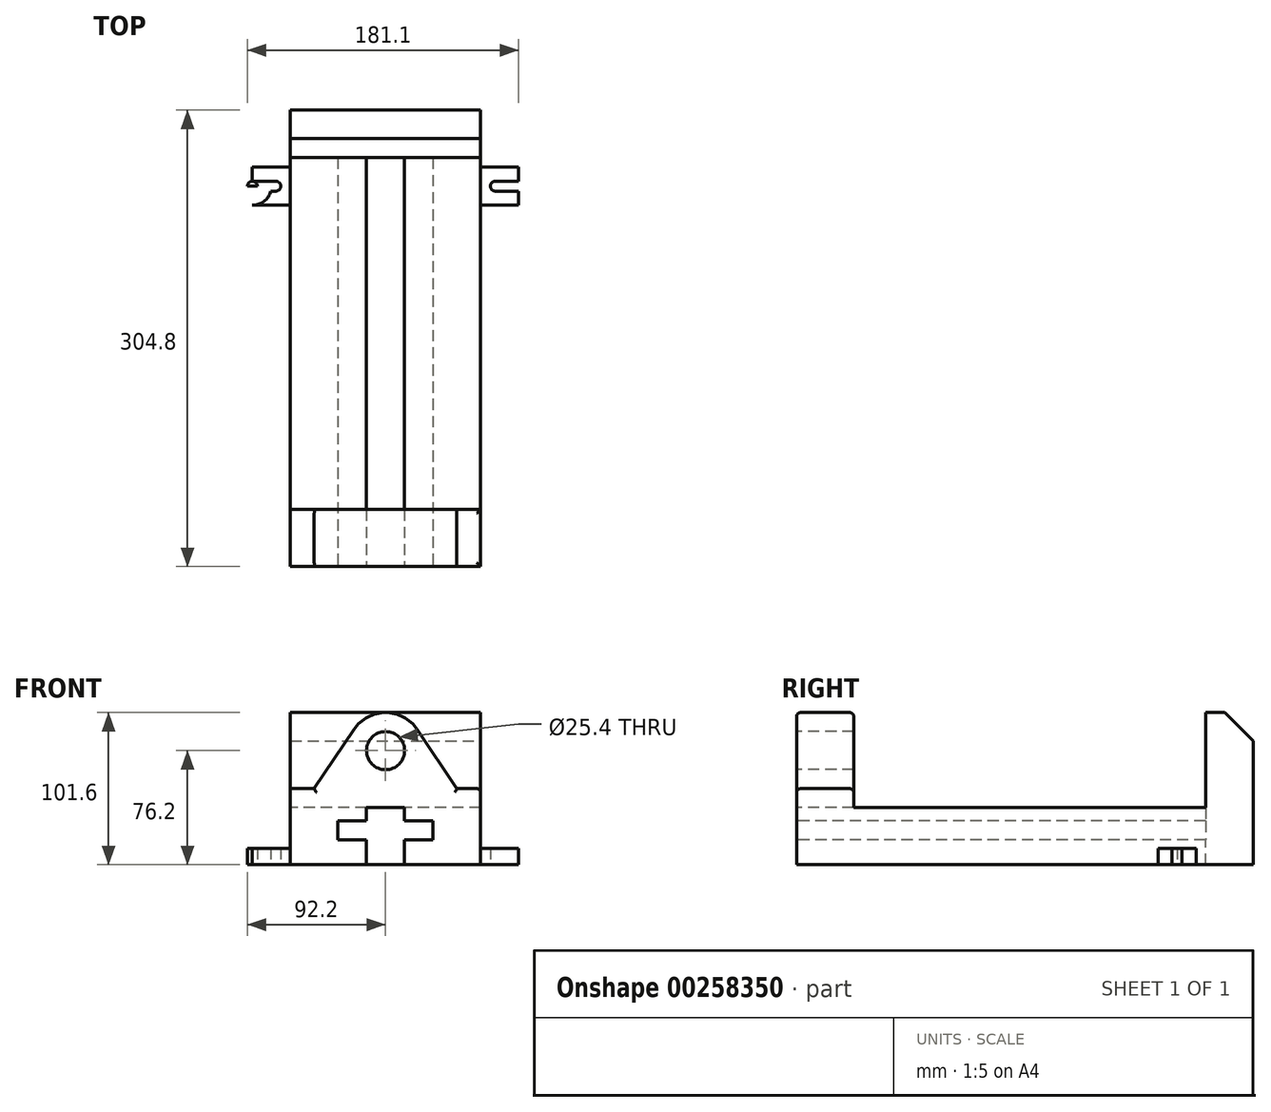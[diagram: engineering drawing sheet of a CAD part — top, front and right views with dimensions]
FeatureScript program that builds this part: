
annotation { "Feature Type Name" : "Feature", "Feature Type Description" : "" }
export const myFeature = defineFeature(function(context is Context, id is Id, definition is map)
    precondition{}
    {
        {
            var Q0;
            Q0=qCreatedBy(makeId("Top.planeOp"),FACE);
            var sketch = newSketch(context, id + "F0", { "sketchPlane" : qUnion([Q0])});
            skLineSegment(sketch, "E0.bottom", {"start": v(63.5, -152.4) * mm, "end": v(-63.5, -152.4) * mm});
            skLineSegment(sketch, "E0.top", {"start": v(63.5, 152.4) * mm, "end": v(-63.5, 152.4) * mm});
            skLineSegment(sketch, "E0.left", {"start": v(63.5, -152.4) * mm, "end": v(63.5, 152.4) * mm});
            skLineSegment(sketch, "E0.right", {"start": v(-63.5, -152.4) * mm, "end": v(-63.5, 152.4) * mm});
            skPoint(sketch, "E0.middle", {"position": v(0, 0) * mm});
            skLineSegment(sketch, "E1", {"start": v(-63.5, 152.4) * mm, "end": v(-63.5, 101.6) * mm});
            skPoint(sketch, "E2.startSnap0", {"position": v(0, 152.4) * mm});
            skLineSegment(sketch, "E3", {"start": v(-63.5, 101.6) * mm, "end": v(-101.6, 101.6) * mm});
            skLineSegment(sketch, "E4", {"start": v(63.5, 101.6) * mm, "end": v(101.6, 101.6) * mm});
            skLineSegment(sketch, "E5", {"start": v(-101.6, 101.6) * mm, "end": v(-88.9, 101.6) * mm});
            skCircle(sketch, "E6", {"center": v(-88.9, 101.6) * mm, "radius": 12.7 * mm});
            skLineSegment(sketch, "E7", {"start": v(-88.9, 101.6) * mm, "end": v(-88.9, 88.9) * mm});
            skLineSegment(sketch, "E8", {"start": v(-88.9, 88.9) * mm, "end": v(-88.9, 101.6) * mm});
            skLineSegment(sketch, "E9", {"start": v(-88.9, 114.3) * mm, "end": v(-88.9, 101.6) * mm});
            skLineSegment(sketch, "E10", {"start": v(-88.9, 88.9) * mm, "end": v(-63.5, 88.9) * mm});
            skLineSegment(sketch, "E11", {"start": v(-88.9, 114.3) * mm, "end": v(-63.5, 114.3) * mm});
            skLineSegment(sketch, "E12", {"start": v(-88.9, 101.6) * mm, "end": v(-88.9, 98.3) * mm});
            skLineSegment(sketch, "E13", {"start": v(-88.9, 98.3) * mm, "end": v(-88.9, 104.9) * mm});
            skCircle(sketch, "E14", {"center": v(-88.9, 101.6) * mm, "radius": 3.3 * mm});
            skLineSegment(sketch, "E15", {"start": v(-88.9, 98.3) * mm, "end": v(-73.28, 98.3) * mm});
            skLineSegment(sketch, "E16", {"start": v(-88.9, 104.9) * mm, "end": v(-73.28, 104.9) * mm});
            skCircle(sketch, "E17", {"center": v(-73.28, 101.6) * mm, "radius": 3.3 * mm});
            skLineSegment(sketch, "E18", {"start": v(101.6, 101.6) * mm, "end": v(88.9, 101.6) * mm});
            skCircle(sketch, "E19", {"center": v(88.9, 101.6) * mm, "radius": 12.7 * mm});
            skCircle(sketch, "E20", {"center": v(88.9, 101.6) * mm, "radius": 3.3 * mm});
            skLineSegment(sketch, "E21", {"start": v(88.9, 101.6) * mm, "end": v(88.9, 88.9) * mm});
            skLineSegment(sketch, "E22", {"start": v(88.9, 88.9) * mm, "end": v(63.5, 88.9) * mm});
            skLineSegment(sketch, "E23", {"start": v(88.9, 101.6) * mm, "end": v(88.9, 114.3) * mm});
            skLineSegment(sketch, "E24", {"start": v(88.9, 114.3) * mm, "end": v(63.5, 114.3) * mm});
            skLineSegment(sketch, "E25", {"start": v(88.9, 101.6) * mm, "end": v(73.28, 101.6) * mm});
            skCircle(sketch, "E26", {"center": v(73.28, 101.6) * mm, "radius": 3.3 * mm});
            skLineSegment(sketch, "E27", {"start": v(73.28, 101.6) * mm, "end": v(73.28, 98.3) * mm});
            skLineSegment(sketch, "E28", {"start": v(73.28, 98.3) * mm, "end": v(88.9, 98.3) * mm});
            skLineSegment(sketch, "E29", {"start": v(73.28, 98.3) * mm, "end": v(73.28, 104.9) * mm});
            skLineSegment(sketch, "E30", {"start": v(73.28, 104.9) * mm, "end": v(88.9, 104.9) * mm});
            skSolve(sketch);
        }
        {
            var Q0;
            Q0=makeQuery(id+"F0.imprint","IMPRINT",FACE,{"disambiguationData":[TD([[makeQuery(id+"F0.imprint","IMPRINT",EDGE,{"derivedFrom":sQuery(id+"F0.wireOp",EDGE,"E0.bottom")}),-1.0]])]});
            extrude(context, id + "F1", {"entities" : qUnion([Q0]), "depth" : 38.1 * mm});
        }
        {
            var Q0;
            Q0=makeQuery(id+"F1.opExtrude","SWEPT_FACE",FACE,{"disambiguationData":[OSD([sQuery(id+"F0.wireOp",EDGE,"E0.bottom")])]});
            var sketch = newSketch(context, id + "F2", { "sketchPlane" : qUnion([Q0])});
            skLineSegment(sketch, "E31", {"start": v(0, 0) * mm, "end": v(12.7, 0) * mm});
            skLineSegment(sketch, "E32", {"start": v(0, 0) * mm, "end": v(-12.7, 0) * mm});
            skLineSegment(sketch, "E33", {"start": v(-12.7, 0) * mm, "end": v(-12.7, 16.51) * mm});
            skLineSegment(sketch, "E34", {"start": v(-12.7, 16.51) * mm, "end": v(-31.75, 16.51) * mm});
            skLineSegment(sketch, "E35", {"start": v(-31.75, 16.51) * mm, "end": v(-31.75, 29.21) * mm});
            skLineSegment(sketch, "E36", {"start": v(-31.75, 29.21) * mm, "end": v(-12.7, 29.21) * mm});
            skLineSegment(sketch, "E37", {"start": v(-12.7, 29.21) * mm, "end": v(-12.7, 38.1) * mm});
            skLineSegment(sketch, "E38", {"start": v(-12.7, 38.1) * mm, "end": v(12.7, 38.1) * mm});
            skLineSegment(sketch, "E39", {"start": v(12.7, 38.1) * mm, "end": v(12.7, 29.21) * mm});
            skLineSegment(sketch, "E40", {"start": v(12.7, 29.21) * mm, "end": v(31.75, 29.21) * mm});
            skLineSegment(sketch, "E41", {"start": v(31.75, 29.21) * mm, "end": v(31.75, 16.51) * mm});
            skLineSegment(sketch, "E42", {"start": v(31.75, 16.51) * mm, "end": v(12.7, 16.51) * mm});
            skLineSegment(sketch, "E43", {"start": v(12.7, 16.51) * mm, "end": v(12.7, 0) * mm});
            skSolve(sketch);
        }
        {
            var Q0;
            Q0 = qSketchRegion(id + "F2", true);
            extrude(context, id + "F3", {"entities" : qUnion([Q0]), "operationType" : NewBodyOperationType.REMOVE, "oppositeDirection" : true, "depth" : 273.05 * mm});
        }
        {
            var Q0;
            Q0=makeQuery(id+"F1.opExtrude","CAP_FACE",FACE,{"disambiguationData":[OSD([sQuery(id+"F0.wireOp",EDGE,"E0.bottom"),sQuery(id+"F0.wireOp",EDGE,"E0.top"),sQuery(id+"F0.wireOp",EDGE,"E0.left"),sQuery(id+"F0.wireOp",EDGE,"E0.right")])],"isStart":false});
            var sketch = newSketch(context, id + "F4", { "sketchPlane" : qUnion([Q0])});
            skLineSegment(sketch, "E44.bottom", {"start": v(-63.5, -152.4) * mm, "end": v(63.5, -152.4) * mm});
            skLineSegment(sketch, "E44.top", {"start": v(-63.5, -114.3) * mm, "end": v(63.5, -114.3) * mm});
            skLineSegment(sketch, "E44.left", {"start": v(-63.5, -152.4) * mm, "end": v(-63.5, -114.3) * mm});
            skLineSegment(sketch, "E44.right", {"start": v(63.5, -152.4) * mm, "end": v(63.5, -114.3) * mm});
            skLineSegment(sketch, "E45.top", {"start": v(-63.5, -184.15) * mm, "end": v(63.5, -184.15) * mm});
            skLineSegment(sketch, "E45.left", {"start": v(-63.5, -152.4) * mm, "end": v(-63.5, -184.15) * mm});
            skLineSegment(sketch, "E45.right", {"start": v(63.5, -152.4) * mm, "end": v(63.5, -184.15) * mm});
            skSolve(sketch);
        }
        {
            var Q0;
            {var subQ0=sQuery(id+"F4.wireOp",EDGE,"E44.bottom");var subQ1=sQuery(id+"F2.wireOp",EDGE,"E38");var subQ2=sQuery(id+"F0.wireOp",EDGE,"E0.bottom");var subQ3=makeQuery(id+"F3.boolean.opBoolean","COPY",EDGE,{"derivedFrom":makeQuery(id+"F3.opExtrude","SWEPT_EDGE",EDGE,{"disambiguationData":[OSD([subQ2,sQuery(id+"F2.wireOp",EDGE,"E37"),subQ1])]})});var subQ4=makeQuery(id+"F4.imprint","INTERSECT",VERTEX,{"derivedFrom":[subQ3,subQ0]});var subQ5=makeQuery(id+"F3.boolean.opBoolean","COPY",EDGE,{"derivedFrom":makeQuery(id+"F3.opExtrude","SWEPT_EDGE",EDGE,{"disambiguationData":[OSD([subQ2,subQ1,sQuery(id+"F2.wireOp",EDGE,"E39")])]})});var subQ6=makeQuery(id+"F4.imprint","INTERSECT",VERTEX,{"derivedFrom":[subQ5,subQ0]});Q0=makeQuery(id+"F4.imprint","IMPRINT",FACE,{"disambiguationData":[TD([[makeQuery(id+"F4.imprint","IMPRINT",EDGE,{"disambiguationData":[TD([[subQ4,-1.0],[subQ6,1.0]])],"derivedFrom":subQ0}),1.0]])]});}
            var Q1;
            {var subQ0=sQuery(id+"F4.wireOp",EDGE,"E44.left");Q1=makeQuery(id+"F4.imprint","IMPRINT",FACE,{"disambiguationData":[TD([[makeQuery(id+"F4.imprint","IMPRINT",EDGE,{"derivedFrom":subQ0}),-1.0]])]});}
            var Q2;
            {var subQ0=sQuery(id+"F4.wireOp",EDGE,"E44.right");Q2=makeQuery(id+"F4.imprint","IMPRINT",FACE,{"disambiguationData":[TD([[makeQuery(id+"F4.imprint","IMPRINT",EDGE,{"derivedFrom":subQ0}),1.0]])]});}
            extrude(context, id + "F5", {"entities" : qUnion([Q0, Q1, Q2]), "operationType" : NewBodyOperationType.ADD, "depth" : 12.7 * mm});
        }
        {
            var Q0;
            {var subQ0=sQuery(id+"F0.wireOp",EDGE,"E0.right");var subQ1=sQuery(id+"F0.wireOp",EDGE,"E0.left");var subQ3=sQuery(id+"F0.wireOp",EDGE,"E0.bottom");var subQ6=makeQuery(id+"F1.opExtrude","SWEPT_FACE",FACE,{"disambiguationData":[OSD([subQ3])]});Q0=makeQuery(id+"F5.boolean.opBoolean","MERGE",FACE,{"derivedFrom":[makeQuery(id+"F3.boolean.opBoolean","SPLIT",FACE,{"disambiguationData":[TD([makeQuery(id+"F1.opExtrude","SWEPT_FACE",FACE,{"disambiguationData":[OSD([subQ1])]})])],"derivedFrom":subQ6}),makeQuery(id+"F3.boolean.opBoolean","SPLIT",FACE,{"disambiguationData":[TD([makeQuery(id+"F1.opExtrude","SWEPT_FACE",FACE,{"disambiguationData":[OSD([subQ0])]})])],"derivedFrom":subQ6}),makeQuery(id+"F5.opExtrude","SWEPT_FACE",FACE,{"disambiguationData":[OSD([sQuery(id+"F4.wireOp",EDGE,"E44.bottom")])]})]});}
            var sketch = newSketch(context, id + "F6", { "sketchPlane" : qUnion([Q0])});
            skLineSegment(sketch, "E46", {"start": v(0, 0) * mm, "end": v(0, 76.2) * mm});
            skPoint(sketch, "E46.endSnap0", {"position": v(0, 50.8) * mm});
            skCircle(sketch, "E47", {"center": v(0, 76.2) * mm, "radius": 12.7 * mm});
            skLineSegment(sketch, "E48", {"start": v(-63.5, 50.8) * mm, "end": v(-47.63, 50.8) * mm});
            skLineSegment(sketch, "E49", {"start": v(63.5, 50.8) * mm, "end": v(47.62, 50.8) * mm});
            skLineSegment(sketch, "E50", {"start": v(47.62, 50.8) * mm, "end": v(21.1, 90.35) * mm});
            skLineSegment(sketch, "E51", {"start": v(-47.63, 50.8) * mm, "end": v(-21.1, 90.35) * mm});
            skArc(sketch, "E52", {"start": v(21.1, 90.35) * mm, "mid": v(0, 101.6) * mm, "end": v(-21.1, 90.35) * mm});
            skLineSegment(sketch, "E53", {"start": v(-63.5, 50.8) * mm, "end": v(-63.5, 38.1) * mm});
            skLineSegment(sketch, "E54", {"start": v(-63.5, 38.1) * mm, "end": v(12.7, 38.1) * mm});
            skPoint(sketch, "E54.endSnap0", {"position": v(12.7, 40) * mm});
            skSolve(sketch);
        }
        {
            var Q0;
            Q0=makeQuery(id+"F6.imprint","IMPRINT",FACE,{"disambiguationData":[TD([[makeQuery(id+"F6.imprint","IMPRINT",EDGE,{"derivedFrom":sQuery(id+"F6.wireOp",EDGE,"E47")}),-1.0]])]});
            extrude(context, id + "F7", {"entities" : qUnion([Q0]), "operationType" : NewBodyOperationType.ADD, "oppositeDirection" : true, "depth" : 38.1 * mm});
        }
        {
            var Q0;
            Q0=makeQuery(id+"F5.opExtrude","CAP_EDGE",EDGE,{"disambiguationData":[OSD([sQuery(id+"F4.wireOp",EDGE,"E44.bottom")])],"isStart":false});
            var Q1;
            Q1=makeQuery(id+"F7.opExtrude","CAP_EDGE",EDGE,{"disambiguationData":[OSD([sQuery(id+"F6.wireOp",EDGE,"E50")])],"isStart":true});
            var Q2;
            Q2=makeQuery(id+"F5.opExtrude","CAP_EDGE",EDGE,{"disambiguationData":[OSD([sQuery(id+"F4.wireOp",EDGE,"E44.right")])],"isStart":false});
            var Q3;
            Q3=makeQuery(id+"F5.opExtrude","CAP_EDGE",EDGE,{"disambiguationData":[OSD([sQuery(id+"F4.wireOp",EDGE,"E44.top")])],"isStart":false});
            var Q4;
            Q4=makeQuery(id+"F7.opExtrude","CAP_EDGE",EDGE,{"disambiguationData":[OSD([sQuery(id+"F6.wireOp",EDGE,"E50")])],"isStart":false});
            var Q5;
            Q5=makeQuery(id+"F7.opExtrude","CAP_EDGE",EDGE,{"disambiguationData":[OSD([sQuery(id+"F6.wireOp",EDGE,"E52")])],"isStart":true});
            var Q6;
            Q6=makeQuery(id+"F7.opExtrude","CAP_EDGE",EDGE,{"disambiguationData":[OSD([sQuery(id+"F6.wireOp",EDGE,"E52")])],"isStart":false});
            var Q7;
            Q7=makeQuery(id+"F7.opExtrude","CAP_EDGE",EDGE,{"disambiguationData":[OSD([sQuery(id+"F6.wireOp",EDGE,"E51")])],"isStart":true});
            var Q8;
            Q8=makeQuery(id+"F7.opExtrude","CAP_EDGE",EDGE,{"disambiguationData":[OSD([sQuery(id+"F6.wireOp",EDGE,"E51")])],"isStart":false});
            var Q9;
            Q9=makeQuery(id+"F7.opExtrude","CAP_EDGE",EDGE,{"disambiguationData":[OSD([sQuery(id+"F6.wireOp",EDGE,"E48")])],"isStart":true});
            var Q10;
            Q10=makeQuery(id+"F7.opExtrude","CAP_EDGE",EDGE,{"disambiguationData":[OSD([sQuery(id+"F6.wireOp",EDGE,"E48")])],"isStart":false});
            var Q11;
            Q11=makeQuery(id+"F7.opExtrude","SWEPT_EDGE",EDGE,{"disambiguationData":[OSD([sQuery(id+"F6.wireOp",EDGE,"E48"),sQuery(id+"F6.wireOp",EDGE,"E53")])]});
            fillet(context, id + "F8", {"entities" : qUnion([Q0, Q1, Q2, Q3, Q4, Q5, Q6, Q7, Q8, Q9, Q10, Q11]), "radius" : 2.54 * mm, "tangentPropagation" : true, "allowEdgeOverflow" : false});
        }
        {
            var Q0;
            Q0=makeQuery(id+"F1.opExtrude","CAP_FACE",FACE,{"disambiguationData":[OSD([sQuery(id+"F0.wireOp",EDGE,"E0.bottom"),sQuery(id+"F0.wireOp",EDGE,"E0.top"),sQuery(id+"F0.wireOp",EDGE,"E0.left"),sQuery(id+"F0.wireOp",EDGE,"E0.right"),sQuery(id+"F0.wireOp",EDGE,"E1")])],"isStart":false});
            var sketch = newSketch(context, id + "F9", { "sketchPlane" : qUnion([Q0])});
            skLineSegment(sketch, "E55", {"start": v(-12.7, 120.65) * mm, "end": v(-63.5, 120.65) * mm});
            skLineSegment(sketch, "E56", {"start": v(-63.5, 120.65) * mm, "end": v(63.5, 120.65) * mm});
            skSolve(sketch);
        }
        {
            var Q0;
            {var subQ0=sQuery(id+"F0.wireOp",EDGE,"E10");Q0=makeQuery(id+"F0.imprint","IMPRINT",FACE,{"disambiguationData":[TD([[makeQuery(id+"F0.imprint","IMPRINT",EDGE,{"derivedFrom":subQ0}),1.0]])]});}
            var Q1;
            {var subQ0=sQuery(id+"F0.wireOp",EDGE,"E8");Q1=makeQuery(id+"F0.imprint","IMPRINT",FACE,{"disambiguationData":[TD([[makeQuery(id+"F0.imprint","IMPRINT",EDGE,{"derivedFrom":subQ0}),-1.0]])]});}
            var Q2;
            {var subQ5=sQuery(id+"F0.wireOp",EDGE,"E8");Q2=makeQuery(id+"F0.imprint","IMPRINT",FACE,{"disambiguationData":[TD([[makeQuery(id+"F0.imprint","IMPRINT",EDGE,{"derivedFrom":subQ5}),1.0]])]});}
            var Q3;
            {var subQ5=sQuery(id+"F0.wireOp",EDGE,"E9");Q3=makeQuery(id+"F0.imprint","IMPRINT",FACE,{"disambiguationData":[TD([[makeQuery(id+"F0.imprint","IMPRINT",EDGE,{"derivedFrom":subQ5}),-1.0]])]});}
            var Q4;
            {var subQ0=sQuery(id+"F0.wireOp",EDGE,"E9");Q4=makeQuery(id+"F0.imprint","IMPRINT",FACE,{"disambiguationData":[TD([[makeQuery(id+"F0.imprint","IMPRINT",EDGE,{"derivedFrom":subQ0}),1.0]])]});}
            var Q5;
            {var subQ0=sQuery(id+"F0.wireOp",EDGE,"E11");Q5=makeQuery(id+"F0.imprint","IMPRINT",FACE,{"disambiguationData":[TD([[makeQuery(id+"F0.imprint","IMPRINT",EDGE,{"derivedFrom":subQ0}),-1.0]])]});}
            extrude(context, id + "F10", {"entities" : qUnion([Q0, Q1, Q2, Q3, Q4, Q5]), "operationType" : NewBodyOperationType.ADD, "depth" : 11.05 * mm});
        }
        {
            var Q0;
            {var subQ0=sQuery(id+"F0.wireOp",EDGE,"E22");Q0=makeQuery(id+"F0.imprint","IMPRINT",FACE,{"disambiguationData":[TD([[makeQuery(id+"F0.imprint","IMPRINT",EDGE,{"derivedFrom":subQ0}),-1.0]])]});}
            var Q1;
            {var subQ1=sQuery(id+"F0.wireOp",EDGE,"E19");var subQ3=sQuery(id+"F0.wireOp",EDGE,"E28");var subQ4=makeQuery(id+"F0.imprint","INTERSECT",VERTEX,{"derivedFrom":[subQ1,subQ3]});Q1=makeQuery(id+"F0.imprint","IMPRINT",FACE,{"disambiguationData":[TD([[makeQuery(id+"F0.imprint","IMPRINT",EDGE,{"disambiguationData":[TD([[subQ4,-1.0]])],"derivedFrom":subQ1}),1.0]])]});}
            var Q2;
            {var subQ0=sQuery(id+"F0.wireOp",EDGE,"E19");var subQ1=sQuery(id+"F0.wireOp",EDGE,"E18");var subQ2=makeQuery(id+"F0.imprint","INTERSECT",VERTEX,{"derivedFrom":[subQ1,subQ0]});Q2=makeQuery(id+"F0.imprint","IMPRINT",FACE,{"disambiguationData":[TD([[makeQuery(id+"F0.imprint","IMPRINT",EDGE,{"disambiguationData":[TD([[subQ2,-1.0]])],"derivedFrom":subQ1}),1.0]])]});}
            var Q3;
            {var subQ0=sQuery(id+"F0.wireOp",EDGE,"E19");var subQ1=sQuery(id+"F0.wireOp",EDGE,"E18");var subQ2=makeQuery(id+"F0.imprint","INTERSECT",VERTEX,{"derivedFrom":[subQ1,subQ0]});Q3=makeQuery(id+"F0.imprint","IMPRINT",FACE,{"disambiguationData":[TD([[makeQuery(id+"F0.imprint","IMPRINT",EDGE,{"disambiguationData":[TD([[subQ2,-1.0]])],"derivedFrom":subQ1}),-1.0]])]});}
            var Q4;
            {var subQ1=sQuery(id+"F0.wireOp",EDGE,"E19");var subQ3=sQuery(id+"F0.wireOp",EDGE,"E30");var subQ4=makeQuery(id+"F0.imprint","INTERSECT",VERTEX,{"derivedFrom":[subQ1,subQ3]});Q4=makeQuery(id+"F0.imprint","IMPRINT",FACE,{"disambiguationData":[TD([[makeQuery(id+"F0.imprint","IMPRINT",EDGE,{"disambiguationData":[TD([[subQ4,1.0]])],"derivedFrom":subQ1}),1.0]])]});}
            var Q5;
            {var subQ0=sQuery(id+"F0.wireOp",EDGE,"E24");Q5=makeQuery(id+"F0.imprint","IMPRINT",FACE,{"disambiguationData":[TD([[makeQuery(id+"F0.imprint","IMPRINT",EDGE,{"derivedFrom":subQ0}),1.0]])]});}
            extrude(context, id + "F11", {"entities" : qUnion([Q0, Q1, Q2, Q3, Q4, Q5]), "operationType" : NewBodyOperationType.ADD, "depth" : 11.05 * mm});
        }
        {
            var Q0;
            {var subQ0=sQuery(id+"F0.wireOp",EDGE,"E0.top");var subQ1=makeQuery(id+"F1.opExtrude","CAP_EDGE",EDGE,{"disambiguationData":[OSD([subQ0])],"isStart":false});Q0=makeQuery(id+"F9.imprint","IMPRINT",FACE,{"disambiguationData":[TD([[makeQuery(id+"F9.imprint","IMPRINT",EDGE,{"derivedFrom":subQ1}),1.0]])]});}
            extrude(context, id + "F12", {"entities" : qUnion([Q0]), "operationType" : NewBodyOperationType.ADD, "depth" : 63.5 * mm});
        }
        {
            var Q0;
            Q0=makeQuery(id+"F12.opExtrude","CAP_EDGE",EDGE,{"disambiguationData":[OSD([sQuery(id+"F0.wireOp",EDGE,"E0.top")])],"isStart":false});
            chamfer(context, id + "F13", {"entities" : qUnion([Q0]), "width" : 19.05 * mm, "tangentPropagation" : true});
        }
    });
